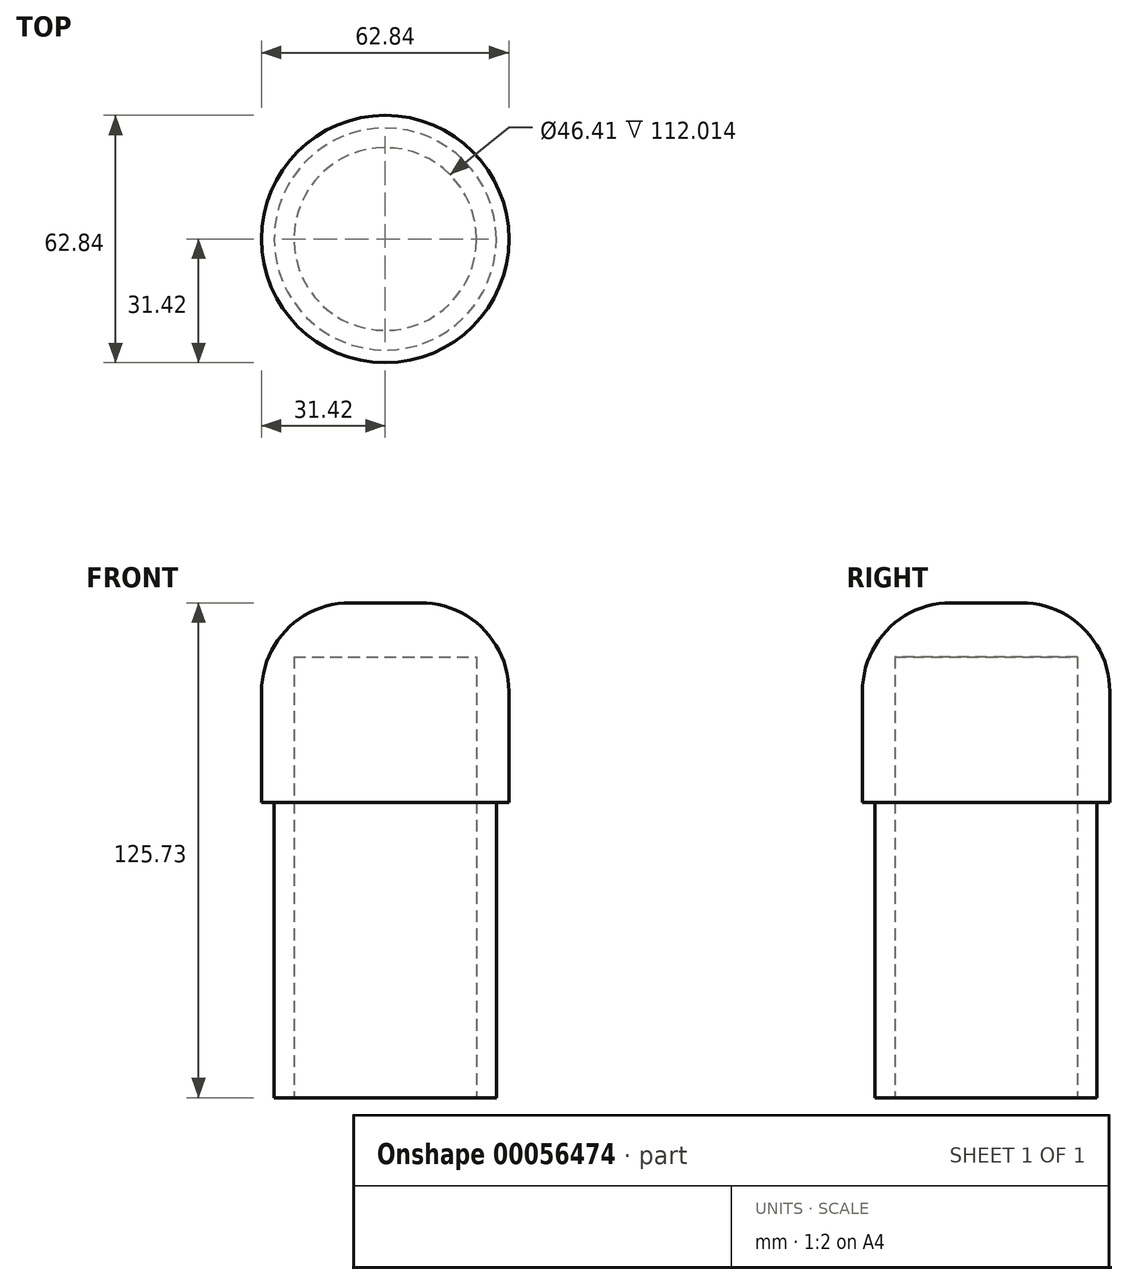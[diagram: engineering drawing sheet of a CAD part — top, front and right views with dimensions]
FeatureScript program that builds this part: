
annotation { "Feature Type Name" : "Feature", "Feature Type Description" : "" }
export const myFeature = defineFeature(function(context is Context, id is Id, definition is map)
    precondition{}
    {
        {
            var Q0;
            Q0=qCreatedBy(makeId("Top.planeOp"),FACE);
            var sketch = newSketch(context, id + "F0", { "sketchPlane" : qUnion([Q0])});
            skCircle(sketch, "E0", {"center": v(0, 0) * mm, "radius": 34.92 * mm});
            skSolve(sketch);
        }
        {
            var Q0;
            Q0=makeQuery(id+"F0.imprint","IMPRINT",FACE,{"disambiguationData":[TD([[makeQuery(id+"F0.imprint","IMPRINT",EDGE,{"derivedFrom":sQuery(id+"F0.wireOp",EDGE,"E0")}),1.0]])]});
            extrude(context, id + "F1", {"entities" : qUnion([Q0]), "depth" : 152.4 * mm});
        }
        {
            var Q0;
            Q0=makeQuery(id+"F1.opExtrude","CAP_EDGE",EDGE,{"disambiguationData":[OSD([sQuery(id+"F0.wireOp",EDGE,"E0")])],"isStart":false});
            fillet(context, id + "F2", {"entities" : qUnion([Q0]), "radius" : 25 * mm, "tangentPropagation" : true, "allowEdgeOverflow" : false});
        }
        {
            var Q0;
            Q0=makeQuery(id+"F1.opExtrude","CAP_FACE",FACE,{"disambiguationData":[OSD([sQuery(id+"F0.wireOp",EDGE,"E0")])],"isStart":true});
            var sketch = newSketch(context, id + "F3", { "sketchPlane" : qUnion([Q0])});
            skCircle(sketch, "E1", {"center": v(0, 0) * mm, "radius": 25.78 * mm});
            skSolve(sketch);
        }
        {
            var Q0;
            Q0=makeQuery(id+"F3.imprint","IMPRINT",FACE,{"disambiguationData":[TD([[makeQuery(id+"F3.imprint","IMPRINT",EDGE,{"derivedFrom":sQuery(id+"F3.wireOp",EDGE,"E1")}),1.0]])]});
            extrude(context, id + "F4", {"entities" : qUnion([Q0]), "operationType" : NewBodyOperationType.REMOVE, "oppositeDirection" : true, "depth" : 137.16 * mm});
        }
        {
            var Q0;
            Q0=makeQuery(id+"F1.opExtrude","CAP_FACE",FACE,{"disambiguationData":[OSD([sQuery(id+"F0.wireOp",EDGE,"E0")])],"isStart":true});
            extrude(context, id + "F5", {"entities" : qUnion([Q0]), "operationType" : NewBodyOperationType.REMOVE, "oppositeDirection" : true, "depth" : 12.7 * mm});
        }
        {
            var Q0;
            Q0=makeQuery(id+"F1.opExtrude","SWEPT_BODY",BODY,{"disambiguationData":[OSD([sQuery(id+"F0.wireOp",EDGE,"E0")])]});
            var Q1;
            Q1=qCreatedBy(makeId("Origin.pointOp"),VERTEX);
            transform(context, id + "F6", {"entities" : qUnion([Q0]), "transformType" : TransformType.SCALE_UNIFORMLY, "scale" : .9, "scalePoint" : qUnion([Q1]), "makeCopy" : false});
        }
        {
            var Q0;
            Q0=makeQuery(id+"F5.boolean.opBoolean","COPY",FACE,{"derivedFrom":makeQuery(id+"F5.opExtrude","CAP_FACE",FACE,{"disambiguationData":[OSD([sQuery(id+"F0.wireOp",EDGE,"E0")])],"isStart":false})});
            extrude(context, id + "F7", {"entities" : qUnion([Q0]), "operationType" : NewBodyOperationType.REMOVE, "oppositeDirection" : true, "depth" : 75 * mm});
        }
        {
            var Q0;
            Q0=makeQuery(id+"F7.boolean.opBoolean","COPY",FACE,{"derivedFrom":makeQuery(id+"F7.opExtrude","CAP_FACE",FACE,{"disambiguationData":[OSD([sQuery(id+"F0.wireOp",EDGE,"E0")])],"isStart":false})});
            var sketch = newSketch(context, id + "F8", { "sketchPlane" : qUnion([Q0])});
            skCircle(sketch, "E2.0", {"center": v(0, 0) * mm, "radius": 28.2 * mm});
            skSolve(sketch);
        }
        {
            var Q0;
            Q0=makeQuery(id+"F8.imprint","IMPRINT",FACE,{"disambiguationData":[TD([[makeQuery(id+"F8.imprint","IMPRINT",EDGE,{"derivedFrom":sQuery(id+"F8.wireOp",EDGE,"E2.0")}),1.0]])]});
            extrude(context, id + "F9", {"entities" : qUnion([Q0]), "operationType" : NewBodyOperationType.ADD, "depth" : 75 * mm});
        }
    });
